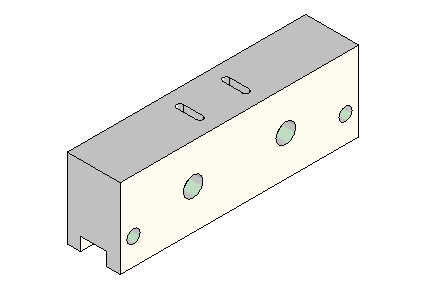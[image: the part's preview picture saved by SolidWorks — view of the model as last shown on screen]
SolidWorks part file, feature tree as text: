
SOLIDWORKS PART (.sldprt)
format: sldprt  version: not decoded by parser v0  size: 195,584 bytes
history: native  units: mm
features: sketch x6, cut_extrude x5, extrude x1 (+11 scaffold rows collapsed)
feature tree (23):
  scaffold x11  (default folders/planes/origin — collapsed)
  sketch  "Sketch1"  dims[D1=114.3mm D2=38.1mm]
  extrude  "Extrude1"  Depth=25.4mm
  sketch  "Sketch2"  dims[D1=12.7mm]
  cut_extrude  "Cut-Extrude1"  Depth=6.35mm
  sketch  "Sketch3"  dims[D1=9.525mm D2=44.45mm]
  cut_extrude  "Cut-Extrude2"  [1 undecoded]
  sketch  "Sketch4"  dims[D1=19.05mm D2=44.45mm]
  cut_extrude  "Cut-Extrude3"  Depth=28.575mm
  sketch  "Sketch5"  dims[c1.D1=~1.502655mm c1.D2=1.5875mm c2.D1=9.525mm c2.D3=19.05mm]
  cut_extrude  "Cut-Extrude4"  Depth=3.175mm
  sketch  "Sketch6"  dims[D1=6.35mm D2=12.7mm D3=101.6mm]
  cut_extrude  "Cut-Extrude5"  [1 undecoded]
decode coverage: 10 of 12 modeling features carry decoded parameters
note: ~ marks probable driven/reference dimensions
note: 2 parameter values undecoded
note: suppression state not decoded; provenance and decode notes live in map.json
